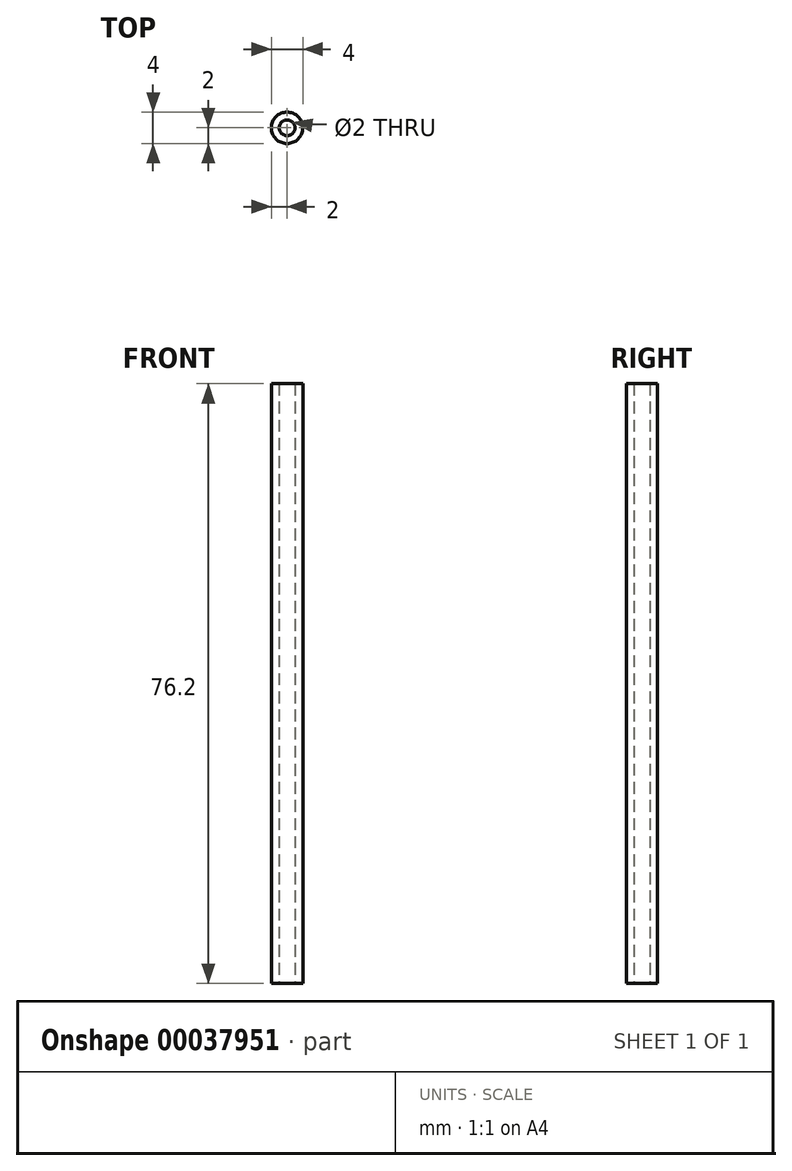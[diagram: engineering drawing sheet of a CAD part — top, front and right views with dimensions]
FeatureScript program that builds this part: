
annotation { "Feature Type Name" : "Feature", "Feature Type Description" : "" }
export const myFeature = defineFeature(function(context is Context, id is Id, definition is map)
    precondition{}
    {
        {
            var Q0;
            Q0=qCreatedBy(makeId("Top.planeOp"),FACE);
            var sketch = newSketch(context, id + "F0", { "sketchPlane" : qUnion([Q0])});
            skCircle(sketch, "E0", {"center": v(0, 0) * mm, "radius": 2 * mm});
            skCircle(sketch, "E1", {"center": v(0, 0) * mm, "radius": 1 * mm});
            skSolve(sketch);
        }
        {
            var Q0;
            Q0 = qSketchRegion(id + "F0", true);
            extrude(context, id + "F1", {"entities" : qUnion([Q0]), "depth" : 76.2 * mm});
        }
    });
